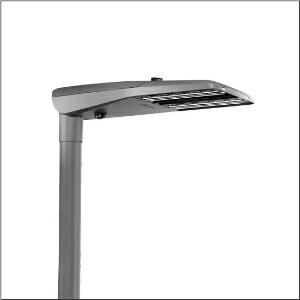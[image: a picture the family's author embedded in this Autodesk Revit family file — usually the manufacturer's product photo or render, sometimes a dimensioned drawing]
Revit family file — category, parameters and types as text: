
# Revit family: streetlight_sl_11_iq_midi___st1_0a_5xc3m51y08le_e71b
name_source: partatom
category: Lighting Fixtures
units: mm (PartAtom-declared; Revit-internal decimal feet)

## family parameters
Cut with Voids When Loaded = No
Host = Face
Light Source = No
Part Type = Normal
Room Calculation Point = No
Round Connector Dimension = Use Diameter
Shared = No

## types (1)
- --- (1 x LED, 8920 lm, 59.4 W, 3000K)
    Apparent Load = 59 VA
    CIE Flux Codes = 33 66 96 100 100
    Color Rendering = 70
    Color Temperature = 3000K
    Default Elevation = 1800 mm
    Description = Streetlight SL 11 iQ midi, mast luminaire, primary light control with 3 zone facetted reflector, of plastic, silver coated, highly specular, primary optical cover: cover, of PMMA, transparent, light distribution: ST1.0a, light emission: direct distribution, primary light characteristic: asymmetric, installation type: post-top, side-entry, LED, High Power LED, rated luminous flux: 8.920lm, luminous efficacy: 150lm/W, light colour: 730, colour temperature: 3000K, control: presetting dimming logarithmic, Street-Remote, Auto-Match, Temp-Guard, Lumen-Switch, Night-Set, Smart-Wire, Light-Fading, Desk-Remote (wireless, voltage-free reading and setting of iQ features in the workshop via application-optimized NFC function/RFID function), optimised constant luminous flux control (CLO 2.0), with cable H07RN-F 5x 1.5mm², mains connection: 230..240V, AC, 50/60Hz, connection cable pre-assembled, cable length: 8,5m, start of lifetime: 59W, end of service life: 62W, reduction: 29W, luminaire housing, of diecast aluminium, powder-coated, Siteco® metallic grey (DB 702S), please order mast flange separately, inclination adjustable without tools: 0°, 5°, 10°, 15° (post-top) | 0°, -5°, -10°, -15° (side-entry), sealing non-destructively replaceable, multi-level sealing system, length: 780mm, width: 376mm, height: 118mm, mast flange for spigot size: 42mm (side-entry): 5XC10008XM4, 60/48mm (side-entry/post-top): 5XC10108XM2, 76/60mm (side-entry/post-top): 5XC10108XM1, equipment: standard, Smart Interface below and above, protection rating (complete): IP66, insulation class (complete): insulation class II (safety insulation), certification: CE, ENEC, VDE, UKCA, impact resistance: IK09, permissible operating ambient temperature for outdoor applications: -25..+50°C, standard-compliant lighting for roads and squares, Environmental Product Declaration (EPD) tested and certified by an independent institute, packaging unit: 1 piece

Light Distribution: ST1.0a
    Height = 118 mm
    Lamp = 1 x LED
    Lamp Light Flux = 8920 lm
    Lamp Power = 59.4 W
    Lamp count = 1
    Length = 780 mm
    Luminous efficacy = 150 lm/W
    Manufacturer = Siteco
    ModVariant = No
    Model = 5XC3M51Y08LE
    Number of Poles = 1
    OnlyDefault = Yes
    Power Factor = 1
    Product Name = Streetlight SL 11 iQ midi | ST1.0a
    Product group = mast luminaire | pylon top
    ProductGroupID = 6100
    Protection Class = Protection class II
    Protection Degree = IP 66
    RLX_Detail_Level = 1
    RLX_Emergency_Light_Flux = 0 lm
    RLX_Emergency_Type = 0
    RLX_Emergency_Type_DB = No
    RlxData = <blob elided: 69097 chars, md5=e837567c>
    Socket = socket
    Standby Power = 0 W
    System Light Flux = 8920 lm
    System Power = 59 W
    Type Comments = factory setting: luminous flux: 100 % | dim-lin: 254 | 521 mA
    Type Image = l_1004429.jpg
    URL = http://relux.com
    VarID = @adj_039417
    Voltage = 0 V
    Weight = 0.00 kg
    Width = 376 mm

## geometry (parser evidence)
native form markers: Blend x4, Sweep x10
no freeform markers — native parametric forms only
